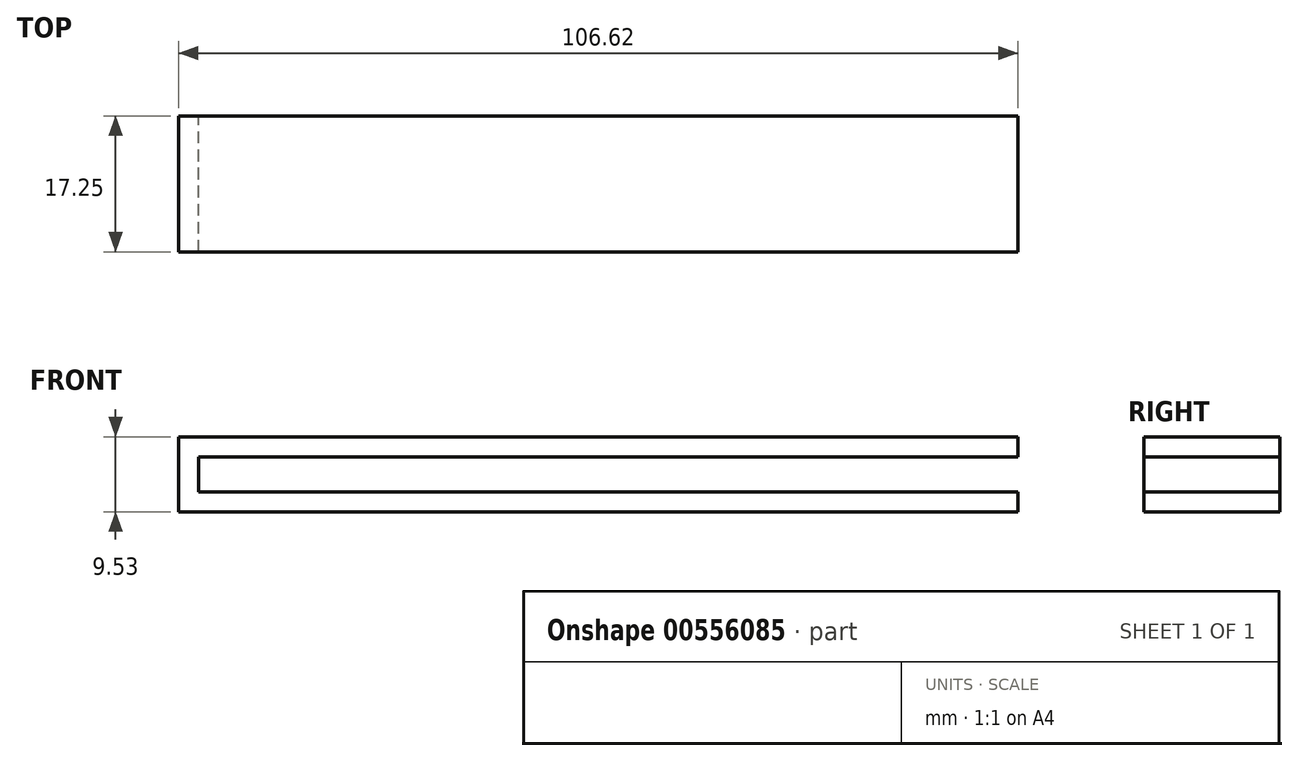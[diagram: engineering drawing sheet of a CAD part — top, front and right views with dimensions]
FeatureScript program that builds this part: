
annotation { "Feature Type Name" : "Feature", "Feature Type Description" : "" }
export const myFeature = defineFeature(function(context is Context, id is Id, definition is map)
    precondition{}
    {
        {
            var Q0;
            Q0=qCreatedBy(makeId("Top.planeOp"),FACE);
            var sketch = newSketch(context, id + "F0", { "sketchPlane" : qUnion([Q0])});
            skLineSegment(sketch, "E0.bottom", {"start": v(-36.3, 36.52) * mm, "end": v(70.32, 36.52) * mm});
            skLineSegment(sketch, "E0.top", {"start": v(-36.3, 53.77) * mm, "end": v(70.32, 53.77) * mm});
            skLineSegment(sketch, "E0.left", {"start": v(-36.3, 36.52) * mm, "end": v(-36.3, 53.77) * mm});
            skLineSegment(sketch, "E0.right", {"start": v(70.32, 36.52) * mm, "end": v(70.32, 53.77) * mm});
            skSolve(sketch);
        }
        {
            var Q0;
            Q0=makeQuery(id+"F0.imprint","IMPRINT",FACE,{"disambiguationData":[TD([[makeQuery(id+"F0.imprint","IMPRINT",EDGE,{"derivedFrom":sQuery(id+"F0.wireOp",EDGE,"E0.bottom")}),1.0]])]});
            extrude(context, id + "F1", {"entities" : qUnion([Q0]), "depth" : 9.52 * mm, "offsetDistance" : 25.4 * mm});
        }
        {
            var Q0;
            Q0=makeQuery(id+"F1.opExtrude","SWEPT_FACE",FACE,{"disambiguationData":[OSD([sQuery(id+"F0.wireOp",EDGE,"E0.bottom")])]});
            var Q1;
            Q1=makeQuery(id+"F1.opExtrude","SWEPT_FACE",FACE,{"disambiguationData":[OSD([sQuery(id+"F0.wireOp",EDGE,"E0.right")])]});
            var Q2;
            Q2=makeQuery(id+"F1.opExtrude","SWEPT_FACE",FACE,{"disambiguationData":[OSD([sQuery(id+"F0.wireOp",EDGE,"E0.top")])]});
            shell(context, id + "F2", {"entities" : qUnion([Q0, Q1, Q2]), "thickness" : 2.54 * mm});
        }
    });
